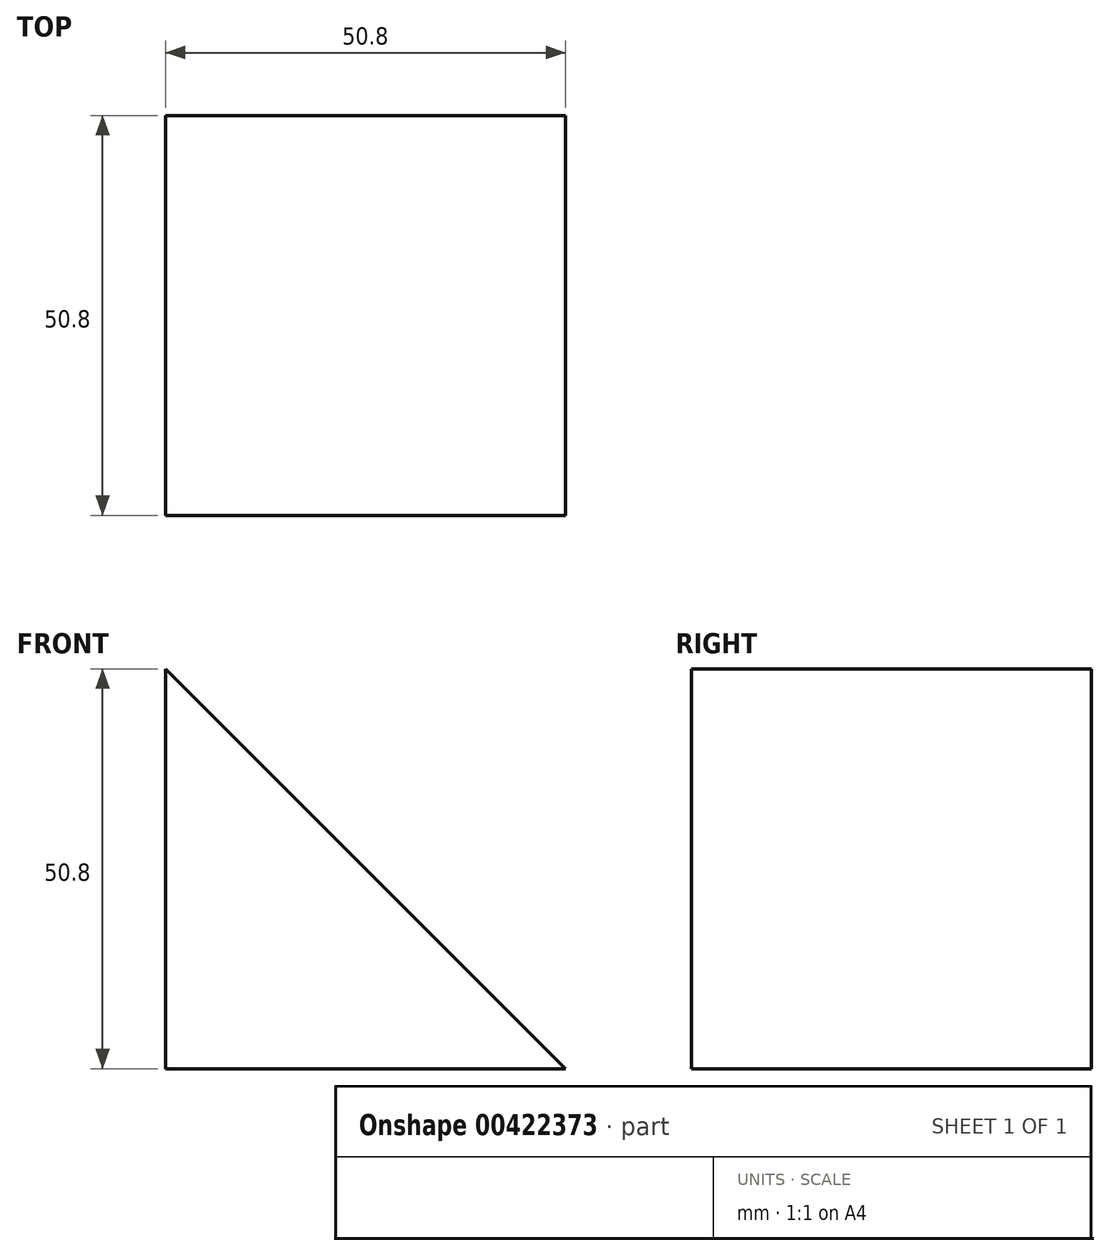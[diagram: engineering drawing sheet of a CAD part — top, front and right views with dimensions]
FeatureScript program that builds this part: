
annotation { "Feature Type Name" : "Feature", "Feature Type Description" : "" }
export const myFeature = defineFeature(function(context is Context, id is Id, definition is map)
    precondition{}
    {
        {
            var Q0;
            Q0=qCreatedBy(makeId("Front.planeOp"),FACE);
            var sketch = newSketch(context, id + "F0", { "sketchPlane" : qUnion([Q0])});
            skLineSegment(sketch, "E0", {"start": v(-51.41, 24.26) * mm, "end": v(-51.41, -26.54) * mm});
            skLineSegment(sketch, "E1", {"start": v(-51.41, -26.54) * mm, "end": v(-0.61, -26.54) * mm});
            skLineSegment(sketch, "E2", {"start": v(-51.41, 24.26) * mm, "end": v(-0.61, -26.54) * mm});
            skSolve(sketch);
        }
        {
            var Q0;
            Q0 = qSketchRegion(id + "F0", true);
            extrude(context, id + "F1", {"entities" : qUnion([Q0]), "depth" : 50.8 * mm});
        }
    });
